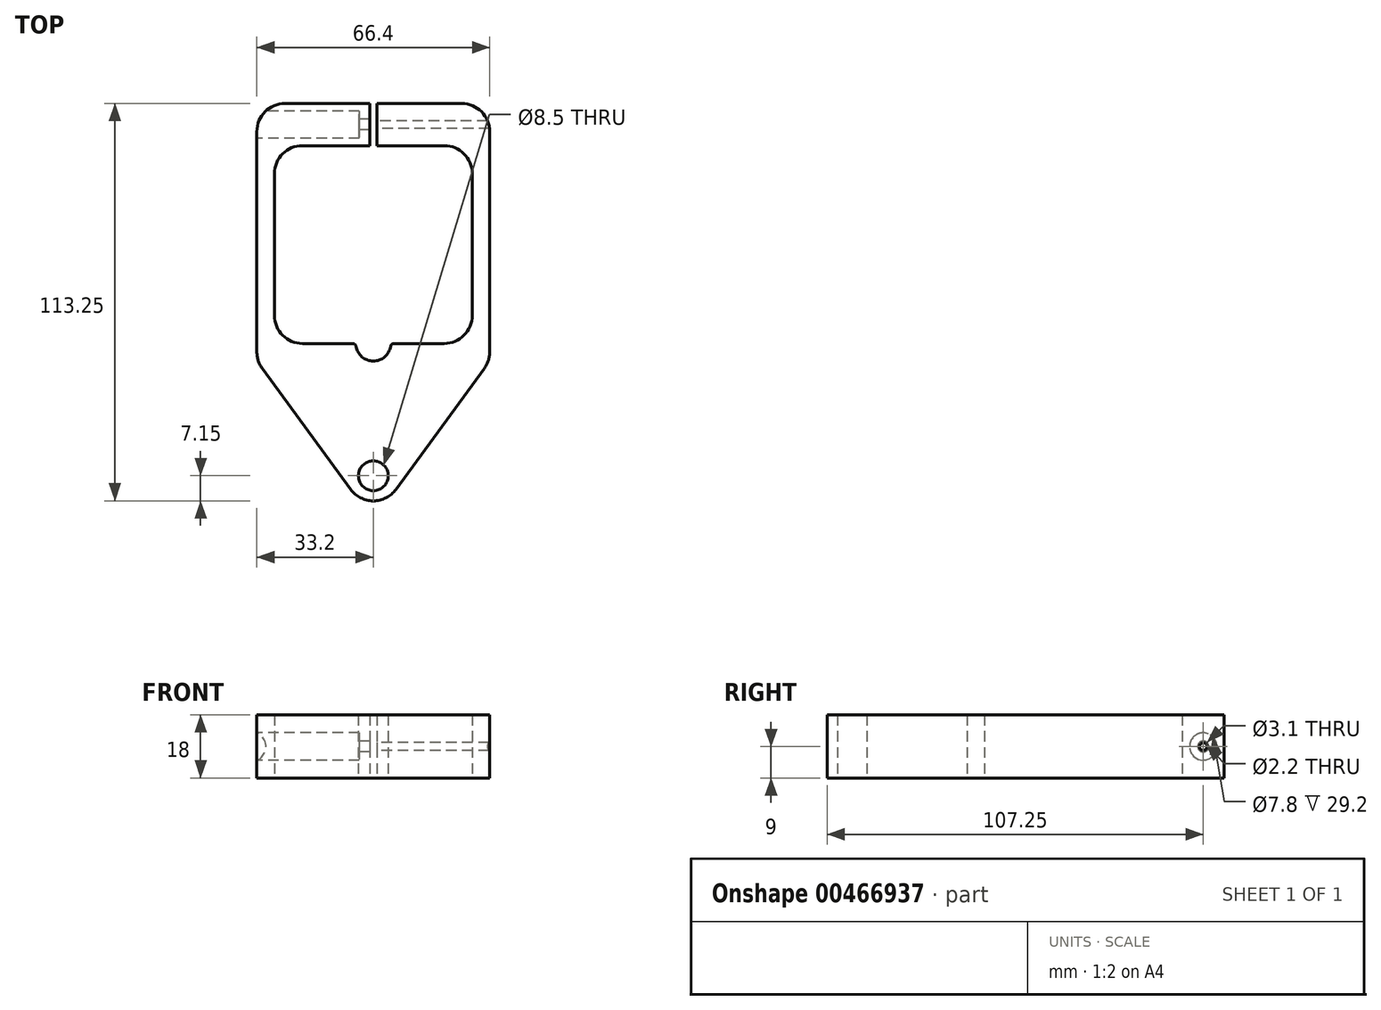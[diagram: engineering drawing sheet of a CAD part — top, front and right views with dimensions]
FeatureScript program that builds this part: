
annotation { "Feature Type Name" : "Feature", "Feature Type Description" : "" }
export const myFeature = defineFeature(function(context is Context, id is Id, definition is map)
    precondition{}
    {
        {
            var Q0;
            Q0=qCreatedBy(makeId("Top.planeOp"),FACE);
            var sketch = newSketch(context, id + "F0", { "sketchPlane" : qUnion([Q0])});
            skLineSegment(sketch, "E0.bottom", {"start": v(33.2, -33.2) * mm, "end": v(32.76, -33.2) * mm});
            skLineSegment(sketch, "E0.left", {"start": v(33.2, -30.59) * mm, "end": v(33.2, 33.2) * mm});
            skLineSegment(sketch, "E0.right", {"start": v(-33.2, -30.59) * mm, "end": v(-33.2, 33.2) * mm});
            skPoint(sketch, "E0.middle", {"position": v(0, 0) * mm});
            skLineSegment(sketch, "E1.bottom", {"start": v(20.2, -28.2) * mm, "end": v(5.92, -28.2) * mm});
            skLineSegment(sketch, "E1.top", {"start": v(20.2, 28.2) * mm, "end": v(1, 28.2) * mm});
            skLineSegment(sketch, "E1.left", {"start": v(28.2, -20.2) * mm, "end": v(28.2, 20.2) * mm});
            skLineSegment(sketch, "E1.right", {"start": v(-28.2, -20.2) * mm, "end": v(-28.2, 20.2) * mm});
            skLineSegment(sketch, "E2", {"start": v(-1, 33.2) * mm, "end": v(-1, 28.2) * mm});
            skLineSegment(sketch, "E3.MirrorCS", {"start": v(1, 33.2) * mm, "end": v(1, 28.2) * mm});
            skLineSegment(sketch, "E4.trimOffspring", {"start": v(-1, 28.2) * mm, "end": v(-20.2, 28.2) * mm});
            skLineSegment(sketch, "E5", {"start": v(-33.2, 32.2) * mm, "end": v(-33.2, 33.2) * mm});
            skLineSegment(sketch, "E6", {"start": v(-25.2, 40.2) * mm, "end": v(-1, 40.2) * mm});
            skLineSegment(sketch, "E7", {"start": v(-1, 40.2) * mm, "end": v(-1, 33.2) * mm});
            skLineSegment(sketch, "E8", {"start": v(1, 33.2) * mm, "end": v(1, 40.2) * mm});
            skLineSegment(sketch, "E9", {"start": v(1, 40.2) * mm, "end": v(25.2, 40.2) * mm});
            skLineSegment(sketch, "E10", {"start": v(33.2, 33.2) * mm, "end": v(33.2, 32.2) * mm});
            skPoint(sketch, "E11.visualSharp", {"position": v(-28.2, 28.2) * mm});
            skArc(sketch, "E11.filletArc", {"start": v(-20.2, 28.2) * mm, "mid": v(-25.86, 25.86) * mm, "end": v(-28.2, 20.2) * mm});
            skPoint(sketch, "E12.visualSharp", {"position": v(28.2, 28.2) * mm});
            skArc(sketch, "E12.filletArc", {"start": v(28.2, 20.2) * mm, "mid": v(25.86, 25.86) * mm, "end": v(20.2, 28.2) * mm});
            skPoint(sketch, "E13.visualSharp", {"position": v(-28.2, -28.2) * mm});
            skArc(sketch, "E13.filletArc", {"start": v(-28.2, -20.2) * mm, "mid": v(-25.86, -25.86) * mm, "end": v(-20.2, -28.2) * mm});
            skPoint(sketch, "E14.visualSharp", {"position": v(28.2, -28.2) * mm});
            skArc(sketch, "E14.filletArc", {"start": v(20.2, -28.2) * mm, "mid": v(25.86, -25.86) * mm, "end": v(28.2, -20.2) * mm});
            skPoint(sketch, "E15.visualSharp", {"position": v(-33.2, 40.2) * mm});
            skArc(sketch, "E15.filletArc", {"start": v(-25.2, 40.2) * mm, "mid": v(-30.86, 37.86) * mm, "end": v(-33.2, 32.2) * mm});
            skPoint(sketch, "E16.visualSharp", {"position": v(33.2, 40.2) * mm});
            skArc(sketch, "E16.filletArc", {"start": v(33.2, 32.2) * mm, "mid": v(30.86, 37.86) * mm, "end": v(25.2, 40.2) * mm});
            skLineSegment(sketch, "E17", {"start": v(0, -28.2) * mm, "end": v(0, -53.2) * mm, "construction": true});
            skLineSegment(sketch, "E18", {"start": v(0, -53.2) * mm, "end": v(0, -78.6) * mm, "construction": true});
            skLineSegment(sketch, "E19", {"start": v(-31.66, -35.3) * mm, "end": v(-6.46, -69.77) * mm});
            skLineSegment(sketch, "E20", {"start": v(6.46, -69.77) * mm, "end": v(31.66, -35.3) * mm});
            skPoint(sketch, "E21.visualSharp", {"position": v(0, -78.6) * mm});
            skArc(sketch, "E21.filletArc", {"start": v(-6.46, -69.77) * mm, "mid": v(0, -73.05) * mm, "end": v(6.46, -69.77) * mm});
            skCircle(sketch, "E22", {"center": v(0, -65.9) * mm, "radius": 4.25 * mm});
            skPoint(sketch, "E23.visualSharp", {"position": v(-33.2, -33.2) * mm});
            skArc(sketch, "E23.filletArc", {"start": v(-33.2, -30.59) * mm, "mid": v(-32.8, -33.07) * mm, "end": v(-31.66, -35.3) * mm});
            skPoint(sketch, "E24.visualSharp", {"position": v(33.2, -33.2) * mm});
            skArc(sketch, "E24.filletArc", {"start": v(31.66, -35.3) * mm, "mid": v(32.8, -33.07) * mm, "end": v(33.2, -30.59) * mm});
            skLineSegment(sketch, "E25.trimOffspring", {"start": v(-32.76, -33.2) * mm, "end": v(-33.2, -33.2) * mm});
            skArc(sketch, "E26", {"start": v(-4.93, -29.03) * mm, "mid": v(0, -33.2) * mm, "end": v(4.93, -29.03) * mm});
            skLineSegment(sketch, "E27.trimOffspring", {"start": v(-5.92, -28.2) * mm, "end": v(-20.2, -28.2) * mm});
            skPoint(sketch, "E28.visualSharp", {"position": v(-5, -28.2) * mm});
            skArc(sketch, "E28.filletArc", {"start": v(-4.93, -29.03) * mm, "mid": v(-5.27, -28.44) * mm, "end": v(-5.92, -28.2) * mm});
            skPoint(sketch, "E29.visualSharp", {"position": v(5, -28.2) * mm});
            skArc(sketch, "E29.filletArc", {"start": v(5.92, -28.2) * mm, "mid": v(5.27, -28.44) * mm, "end": v(4.93, -29.03) * mm});
            skSolve(sketch);
        }
        {
            var Q0;
            {var subQ3=sQuery(id+"F0.wireOp",EDGE,"E0.left");Q0=makeQuery(id+"F0.imprint","IMPRINT",FACE,{"disambiguationData":[TD([[makeQuery(id+"F0.imprint","IMPRINT",EDGE,{"derivedFrom":subQ3}),1.0]])]});}
            extrude(context, id + "F1", {"entities" : qUnion([Q0]), "depth" : 18 * mm, "offsetDistance" : 25 * mm});
        }
        {
            var Q0;
            Q0=makeQuery(id+"F1.opExtrude","SWEPT_FACE",FACE,{"disambiguationData":[OSD([sQuery(id+"F0.wireOp",EDGE,"E0.right")])]});
            var sketch = newSketch(context, id + "F2", { "sketchPlane" : qUnion([Q0])});
            skPoint(sketch, "E30.0", {"position": v(-34.2, 0) * mm});
            skLineSegment(sketch, "E31", {"start": v(-34.2, 0) * mm, "end": v(-34.2, 10.94) * mm, "construction": true});
            skLineSegment(sketch, "E32", {"start": v(-32.2, 9) * mm, "end": v(-40.78, 9) * mm, "construction": true});
            skCircle(sketch, "E33", {"center": v(-34.2, 9) * mm, "radius": 1.1 * mm});
            skCircle(sketch, "E34", {"center": v(-34.2, 9) * mm, "radius": 3.9 * mm});
            skCircle(sketch, "E35", {"center": v(-34.2, 9) * mm, "radius": 1.55 * mm});
            skSolve(sketch);
        }
        {
            var Q0;
            Q0=makeQuery(id+"F2.imprint","IMPRINT",FACE,{"disambiguationData":[TD([[makeQuery(id+"F2.imprint","IMPRINT",EDGE,{"derivedFrom":sQuery(id+"F2.wireOp",EDGE,"E33")}),1.0]])]});
            extrude(context, id + "F3", {"entities" : qUnion([Q0]), "operationType" : NewBodyOperationType.REMOVE, "endBound" : BoundingType.THROUGH_ALL, "oppositeDirection" : true, "depth" : 25 * mm});
        }
        {
            var Q0;
            Q0=makeQuery(id+"F2.imprint","IMPRINT",FACE,{"disambiguationData":[TD([[makeQuery(id+"F2.imprint","IMPRINT",EDGE,{"derivedFrom":sQuery(id+"F2.wireOp",EDGE,"E33")}),-1.0]])]});
            extrude(context, id + "F4", {"entities" : qUnion([Q0]), "operationType" : NewBodyOperationType.REMOVE, "oppositeDirection" : true, "depth" : 33.2 * mm});
        }
        {
            var Q0;
            Q0=makeQuery(id+"F2.imprint","IMPRINT",FACE,{"disambiguationData":[TD([[makeQuery(id+"F2.imprint","IMPRINT",EDGE,{"derivedFrom":sQuery(id+"F2.wireOp",EDGE,"E35")}),-1.0]])]});
            var Q1;
            {var subQ0=sQuery(id+"F2.wireOp",EDGE,"E34");var subQ1=makeQuery(id+"F1.opExtrude","SWEPT_EDGE",EDGE,{"disambiguationData":[OSD([sQuery(id+"F0.wireOp",EDGE,"E0.right"),sQuery(id+"F0.wireOp",EDGE,"E15.filletArc")])]});var subQ2=makeQuery(id+"F2.imprint","INTERSECT",VERTEX,{"disambiguationData":[OD(0.0)],"derivedFrom":[subQ1,subQ0]});Q1=makeQuery(id+"F2.imprint","IMPRINT",FACE,{"disambiguationData":[TD([[makeQuery(id+"F2.imprint","IMPRINT",EDGE,{"disambiguationData":[TD([[subQ2,-1.0]])],"derivedFrom":subQ0}),1.0]])]});}
            extrude(context, id + "F5", {"entities" : qUnion([Q0, Q1]), "operationType" : NewBodyOperationType.REMOVE, "oppositeDirection" : true, "depth" : 29.2 * mm});
        }
    });
